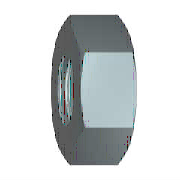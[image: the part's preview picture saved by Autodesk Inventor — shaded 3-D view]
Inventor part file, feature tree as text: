
AUTODESK INVENTOR PART (.ipt)
format: ipt  version: 2020 (Build 240168000, 168)  size: 169,984 bytes
history: native  units: mm (DEFAULTED — no unit token found)
features: sketch x3, extrude x1, chamfer x1, hole x1, other x1, plane x1
ambient origin geometry x7: Origin, YZ Plane, XZ Plane, X Axis, Y Axis, Z Axis, Center Point
bodies: Solid1 (feature_tree)
feature tree (8):
  extrude  "轴承体"  Depth=9.3mm
  chamfer  "倒角1"  Angle=30.0deg  [1 undecoded]
  hole  "螺纹"  [1 undecoded]
  other  "Work Axis1"
  plane  "Work Plane1"
  sketch  "草图1"  dims[d0=18.475209mm d1=9.3mm]
  sketch  "草图2"  dims[d2=0.0mm]
  sketch  "草图3"  dims[d3=30.0deg d4=30.0deg d5=16.0mm d6=16.0mm d7=90.0deg d25=8.376mm d26=6.0mm d27=4.0mm d28=2.0mm d29=14.3117mm d30=8.0mm d31=20.594885mm d8=0.811899mm d9=30.0deg d10=0.811899mm d11=30.0deg d13=0.0mm d14=0.0mm d39=0.0mm d40=0.811899mm d41=0.811899mm d42=0.0mm]
note: 2 required parameter values undecoded (feature->parameter linkage not recoverable at this tier; creation-order binding heuristic only, values carry confidence <= 0.55)
